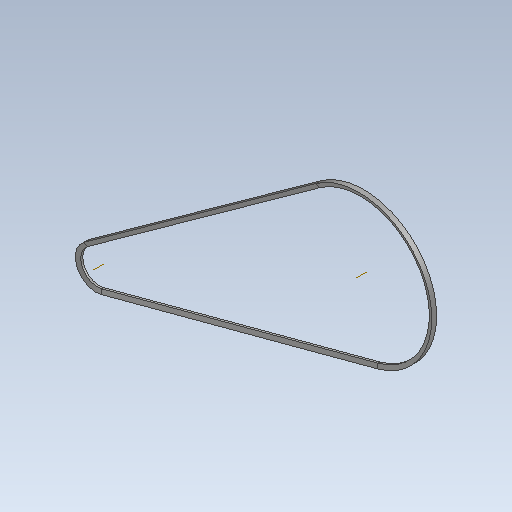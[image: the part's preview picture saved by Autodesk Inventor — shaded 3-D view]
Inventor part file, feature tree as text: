
AUTODESK INVENTOR PART (.ipt)
format: ipt  version: 2020.5 (Build 245400000, 400)  size: 97,792 bytes
history: native  units: mm (DEFAULTED — no unit token found)
features: other x5, sweep x1
ambient origin geometry x8: Origin, YZ Plane, XZ Plane, XY Plane, X Axis, Y Axis, Z Axis, Center Point
bodies: Solid1 (feature_tree)
feature tree (6):
  other  "Trayectoria de boceto"
  other  "Plano de sección transversal"
  other  "Eje de trabajo1"
  other  "Eje de trabajo2"
  sweep  "Correa"
  other  "Sección transversal"
